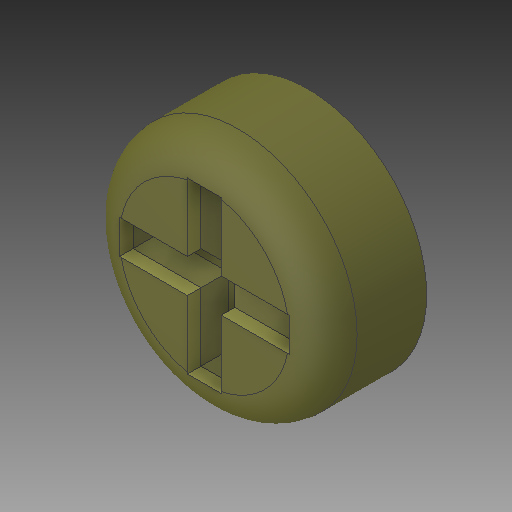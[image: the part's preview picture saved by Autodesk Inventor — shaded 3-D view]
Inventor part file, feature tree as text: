
AUTODESK INVENTOR PART (.ipt)
format: ipt  version: 2019 (Build 230136000, 136)  size: 158,208 bytes
history: mixed  units: mm
features: chamfer x1, imported_body x1
ambient origin geometry x8: Origin, YZ Plane, XZ Plane, XY Plane, X Axis, Y Axis, Z Axis, Center Point
bodies: Solid1 (imported_parasolid)
feature tree (2):
  chamfer  "Chamfer1"  [1 undecoded]
  imported_body  NMx_Import_Brep_tag  [imported B-rep: ~17 faces, bbox_mm=[2.974745, 2.474745, 0.5]]
note: 1 required parameter value undecoded (feature->parameter linkage not recoverable at this tier; creation-order binding heuristic only, values carry confidence <= 0.55)
